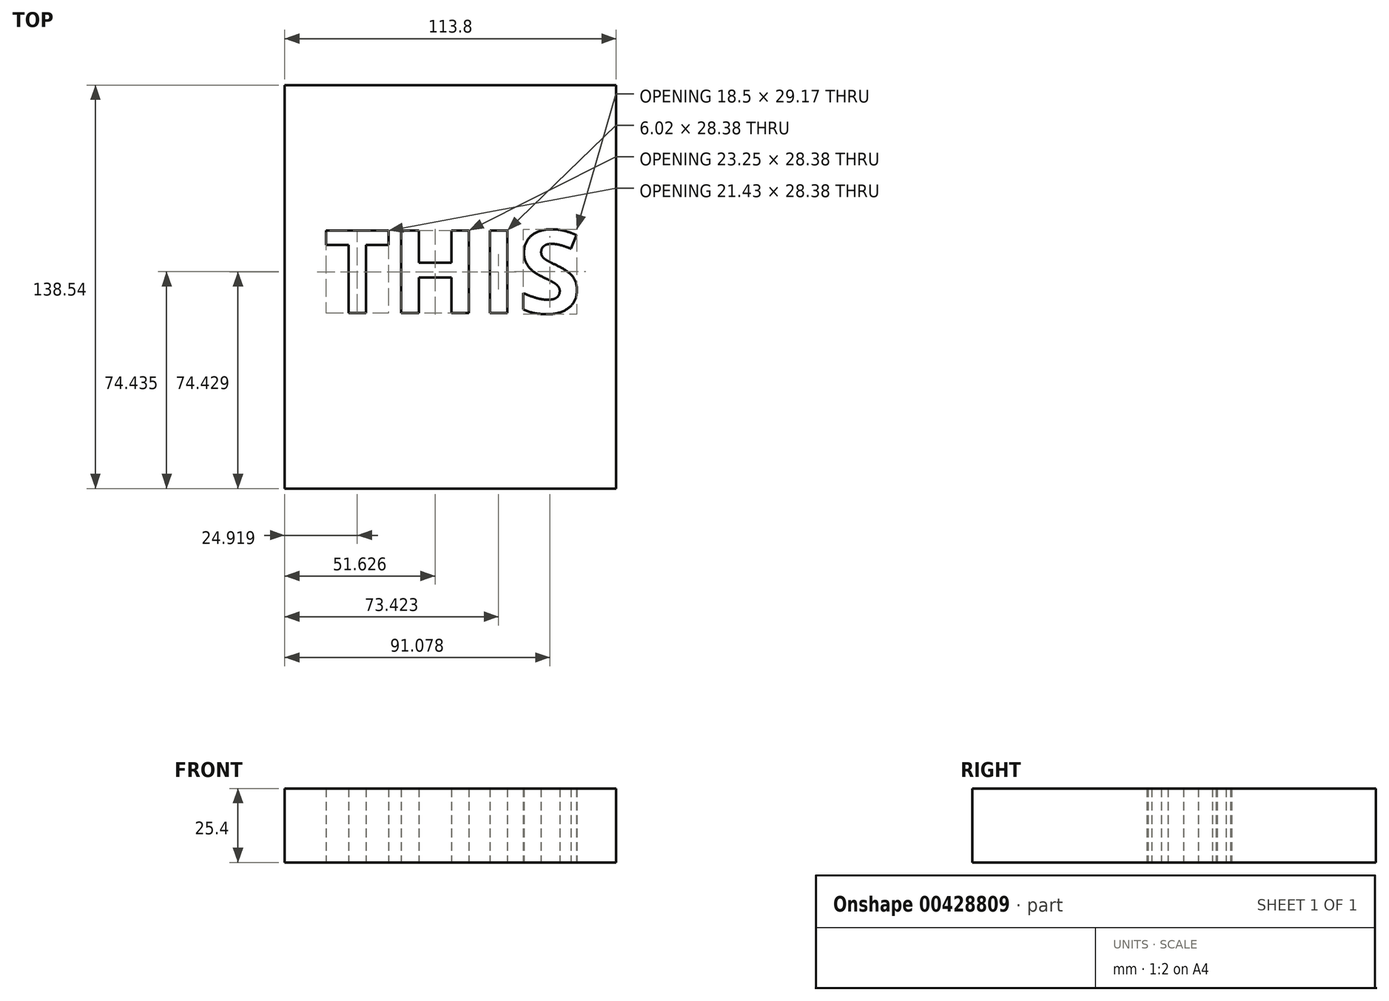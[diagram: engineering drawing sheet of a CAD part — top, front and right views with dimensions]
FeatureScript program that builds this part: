
annotation { "Feature Type Name" : "Feature", "Feature Type Description" : "" }
export const myFeature = defineFeature(function(context is Context, id is Id, definition is map)
    precondition{}
    {
        {
            var Q0;
            Q0=qCreatedBy(makeId("Top.planeOp"),FACE);
            var sketch = newSketch(context, id + "F0", { "sketchPlane" : qUnion([Q0])});
            skLineSegment(sketch, "E0.bottom", {"start": v(56.9, 69.27) * mm, "end": v(-56.9, 69.27) * mm});
            skLineSegment(sketch, "E0.top", {"start": v(56.9, -69.27) * mm, "end": v(-56.9, -69.27) * mm});
            skLineSegment(sketch, "E0.left", {"start": v(56.9, 69.27) * mm, "end": v(56.9, -69.27) * mm});
            skLineSegment(sketch, "E0.right", {"start": v(-56.9, 69.27) * mm, "end": v(-56.9, -69.27) * mm});
            skPoint(sketch, "E0.middle", {"position": v(0, 0) * mm});
            skText(sketch, "E1", { "text": "THIS", "fontName": "OpenSans-Bold.ttf"});
            const initialGuessF0  = {"E1": [-0.04349, -0.00903, 1, 0, 0.02862]};
            skSetInitialGuess(sketch, initialGuessF0);
            skSolve(sketch);
        }
        {
            var Q0;
            Q0=makeQuery(id+"F0.imprint","IMPRINT",FACE,{"disambiguationData":[TD([[makeQuery(id+"F0.imprint","IMPRINT",EDGE,{"derivedFrom":sQuery(id+"F0.wireOp",EDGE,"E0.bottom")}),1.0]])]});
            extrude(context, id + "F1", {"entities" : qUnion([Q0]), "depth" : 25.4 * mm, "offsetDistance" : 25.4 * mm});
        }
    });
